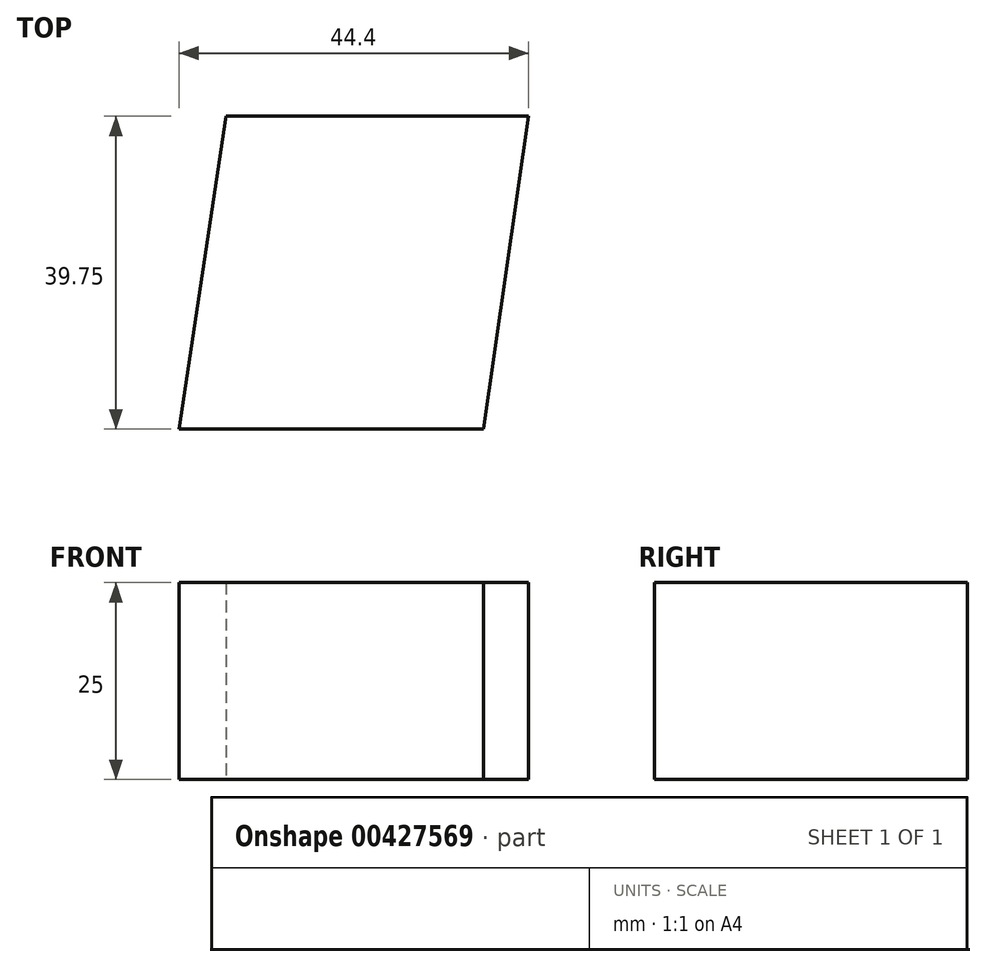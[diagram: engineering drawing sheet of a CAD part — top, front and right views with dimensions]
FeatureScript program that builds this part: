
annotation { "Feature Type Name" : "Feature", "Feature Type Description" : "" }
export const myFeature = defineFeature(function(context is Context, id is Id, definition is map)
    precondition{}
    {
        {
            var Q0;
            Q0=qCreatedBy(makeId("Top.planeOp"),FACE);
            var sketch = newSketch(context, id + "F0", { "sketchPlane" : qUnion([Q0])});
            skLineSegment(sketch, "E0", {"start": v(-20.7, 39.75) * mm, "end": v(-26.7, 0) * mm});
            skLineSegment(sketch, "E1", {"start": v(-26.7, 0) * mm, "end": v(12, 0) * mm});
            skLineSegment(sketch, "E2", {"start": v(12, 0) * mm, "end": v(17.7, 39.75) * mm});
            skLineSegment(sketch, "E3", {"start": v(17.7, 39.75) * mm, "end": v(-20.7, 39.75) * mm});
            skLineSegment(sketch, "E4.bottom", {"start": v(-8.4, 24.45) * mm, "end": v(0, 24.45) * mm});
            skLineSegment(sketch, "E4.top", {"start": v(-8.4, 16.65) * mm, "end": v(0, 16.65) * mm});
            skLineSegment(sketch, "E4.left", {"start": v(-8.4, 24.45) * mm, "end": v(-8.4, 16.65) * mm});
            skLineSegment(sketch, "E4.right", {"start": v(0, 24.45) * mm, "end": v(0, 16.65) * mm});
            skSolve(sketch);
        }
        {
            var Q0;
            Q0=makeQuery(id+"F0.imprint","IMPRINT",FACE,{"disambiguationData":[TD([[makeQuery(id+"F0.imprint","IMPRINT",EDGE,{"derivedFrom":sQuery(id+"F0.wireOp",EDGE,"E4.bottom")}),-1.0]])]});
            var Q1;
            Q1=makeQuery(id+"F0.imprint","IMPRINT",FACE,{"disambiguationData":[TD([[makeQuery(id+"F0.imprint","IMPRINT",EDGE,{"derivedFrom":sQuery(id+"F0.wireOp",EDGE,"E0")}),1.0]])]});
            extrude(context, id + "F1", {"entities" : qUnion([Q0, Q1]), "depth" : 25 * mm});
        }
    });
